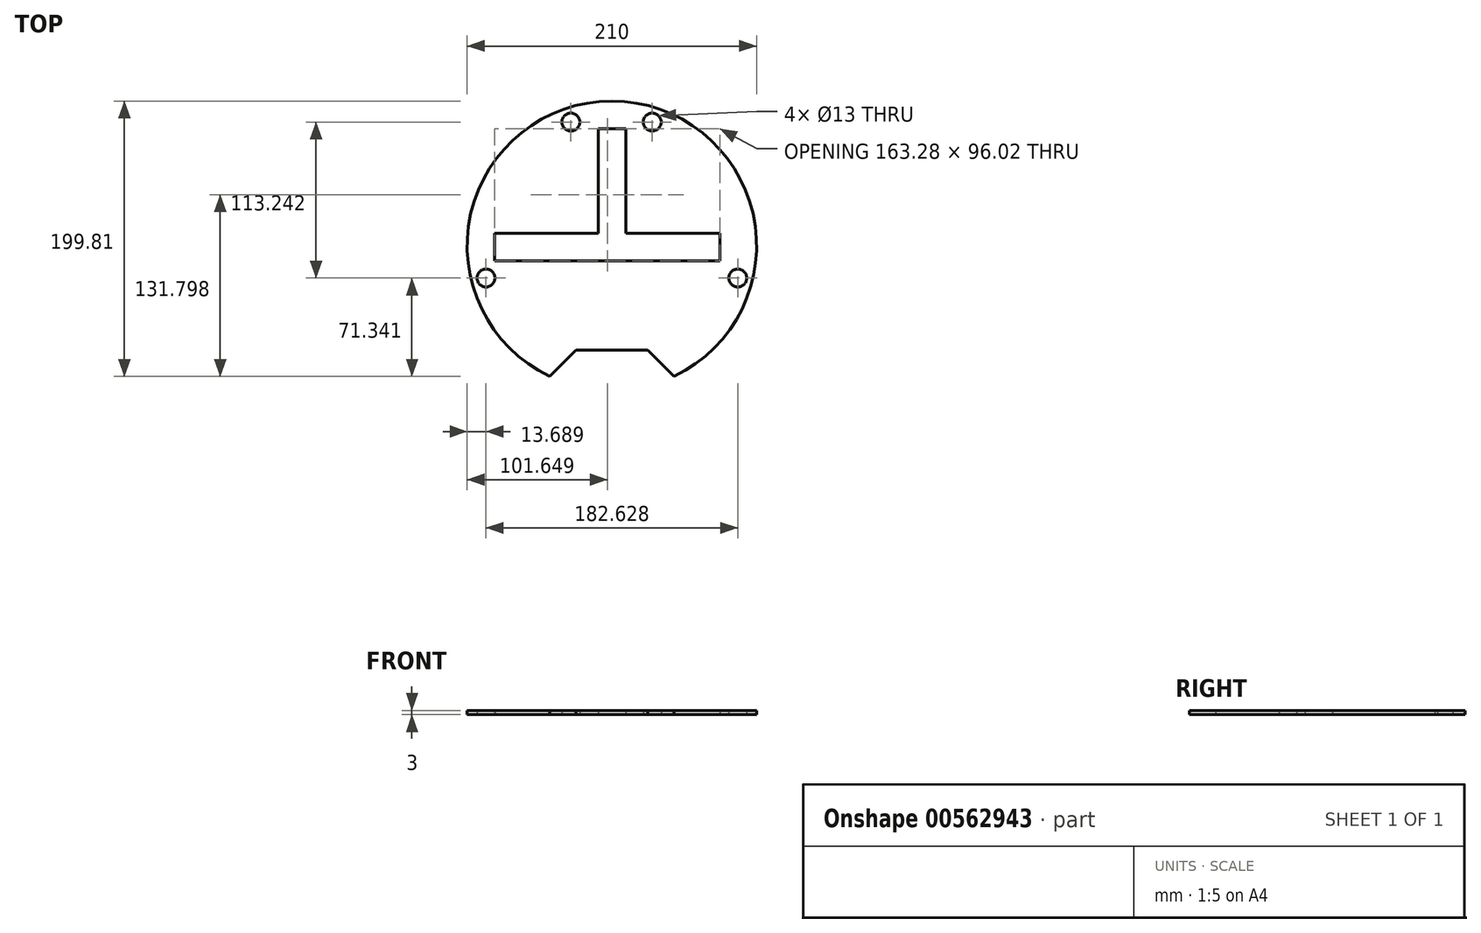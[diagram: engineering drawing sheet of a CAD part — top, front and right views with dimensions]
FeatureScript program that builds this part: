
annotation { "Feature Type Name" : "Feature", "Feature Type Description" : "" }
export const myFeature = defineFeature(function(context is Context, id is Id, definition is map)
    precondition{}
    {
        {
            var Q0;
            Q0=qCreatedBy(makeId("Top.planeOp"),FACE);
            var sketch = newSketch(context, id + "F0", { "sketchPlane" : qUnion([Q0])});
            skCircle(sketch, "E0", {"center": v(-0.03, 1.02) * mm, "radius": 105 * mm});
            skCircle(sketch, "E1", {"center": v(-29.75, 90.8) * mm, "radius": 6.5 * mm});
            skCircle(sketch, "E2", {"center": v(29.27, 90.8) * mm, "radius": 6.5 * mm});
            skCircle(sketch, "E3", {"center": v(-91.34, -22.45) * mm, "radius": 6.5 * mm});
            skCircle(sketch, "E4", {"center": v(91.29, -22.45) * mm, "radius": 6.5 * mm});
            skLineSegment(sketch, "E5", {"start": v(-26.15, -74.78) * mm, "end": v(26.1, -74.78) * mm});
            skLineSegment(sketch, "E6", {"start": v(-26.15, -74.78) * mm, "end": v(-45.16, -93.79) * mm});
            skLineSegment(sketch, "E7", {"start": v(26.1, -74.78) * mm, "end": v(45.1, -93.79) * mm});
            skLineSegment(sketch, "E8", {"start": v(-85.02, 0) * mm, "end": v(-85.02, 10) * mm});
            skLineSegment(sketch, "E9", {"start": v(-85.02, 10) * mm, "end": v(-85.02, -10) * mm});
            skLineSegment(sketch, "E10", {"start": v(78.26, 0) * mm, "end": v(78.26, -10) * mm});
            skLineSegment(sketch, "E11", {"start": v(78.26, -10) * mm, "end": v(78.26, 10) * mm});
            skLineSegment(sketch, "E12", {"start": v(78.26, -10) * mm, "end": v(-85.02, -10) * mm});
            skLineSegment(sketch, "E13", {"start": v(0, 86.02) * mm, "end": v(10, 86.02) * mm});
            skLineSegment(sketch, "E14", {"start": v(10, 86.02) * mm, "end": v(-10, 86.02) * mm});
            skLineSegment(sketch, "E15", {"start": v(-10, 86.02) * mm, "end": v(-10, 10) * mm});
            skLineSegment(sketch, "E16", {"start": v(10, 10) * mm, "end": v(78.26, 10) * mm});
            skLineSegment(sketch, "E17", {"start": v(-10, 10) * mm, "end": v(-85.02, 10) * mm});
            skLineSegment(sketch, "E18", {"start": v(10, 86.02) * mm, "end": v(10, 10) * mm});
            skSolve(sketch);
        }
        {
            var Q0;
            Q0=makeQuery(id+"F0.imprint","IMPRINT",FACE,{"disambiguationData":[TD([[makeQuery(id+"F0.imprint","IMPRINT",EDGE,{"derivedFrom":sQuery(id+"F0.wireOp",EDGE,"E1")}),-1.0]])]});
            extrude(context, id + "F1", {"entities" : qUnion([Q0]), "depth" : 3 * mm, "offsetDistance" : 25.4 * mm});
        }
    });
